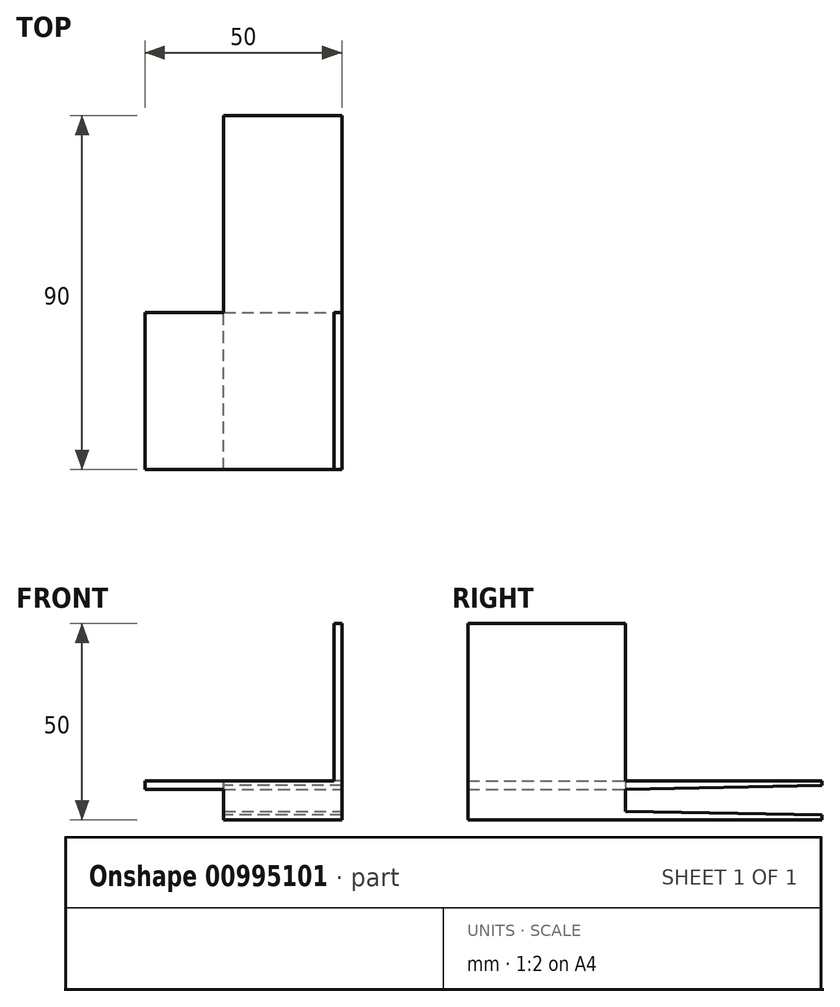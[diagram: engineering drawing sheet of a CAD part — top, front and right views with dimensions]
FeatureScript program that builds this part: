
annotation { "Feature Type Name" : "Feature", "Feature Type Description" : "" }
export const myFeature = defineFeature(function(context is Context, id is Id, definition is map)
    precondition{}
    {
        {
            var Q0;
            Q0=qCreatedBy(makeId("Front.planeOp"),FACE);
            var sketch = newSketch(context, id + "F0", { "sketchPlane" : qUnion([Q0])});
            skLineSegment(sketch, "E0.bottom", {"start": v(0, 0) * mm, "end": v(30, 0) * mm});
            skLineSegment(sketch, "E0.top", {"start": v(0, 10) * mm, "end": v(30, 10) * mm});
            skLineSegment(sketch, "E0.left", {"start": v(0, 0) * mm, "end": v(0, 10) * mm});
            skLineSegment(sketch, "E0.right", {"start": v(30, 0) * mm, "end": v(30, 10) * mm});
            skSolve(sketch);
        }
        {
            var Q0;
            Q0=qSketchRegion(id+"F0",true);
            extrude(context, id + "F1", {"entities" : qUnion([Q0]), "depth" : 40 * mm, "offsetDistance" : 25 * mm});
        }
        {
            var Q0;
            Q0=makeQuery(id+"F1.opExtrude","CAP_FACE",FACE,{"disambiguationData":[OSD([sQuery(id+"F0.wireOp",EDGE,"E0.bottom"),sQuery(id+"F0.wireOp",EDGE,"E0.top"),sQuery(id+"F0.wireOp",EDGE,"E0.left"),sQuery(id+"F0.wireOp",EDGE,"E0.right")])],"isStart":true});
            var sketch = newSketch(context, id + "F2", { "sketchPlane" : qUnion([Q0])});
            skLineSegment(sketch, "E1.bottom", {"start": v(0, 0) * mm, "end": v(-30, 0) * mm});
            skLineSegment(sketch, "E1.top", {"start": v(0, 2.25) * mm, "end": v(-30, 2.25) * mm});
            skLineSegment(sketch, "E1.left", {"start": v(0, 0) * mm, "end": v(0, 2.25) * mm});
            skLineSegment(sketch, "E1.right", {"start": v(-30, 0) * mm, "end": v(-30, 2.25) * mm});
            skLineSegment(sketch, "E2.bottom", {"start": v(0, 10) * mm, "end": v(-30, 10) * mm});
            skLineSegment(sketch, "E2.top", {"start": v(0, 7.75) * mm, "end": v(-30, 7.75) * mm});
            skLineSegment(sketch, "E2.left", {"start": v(0, 10) * mm, "end": v(0, 7.75) * mm});
            skLineSegment(sketch, "E2.right", {"start": v(-30, 10) * mm, "end": v(-30, 7.75) * mm});
            skLineSegment(sketch, "E3", {"start": v(0, 2.25) * mm, "end": v(0, 7.75) * mm});
            skSolve(sketch);
        }
        {
            var Q0;
            Q0=qSketchRegion(id+"F2",true);
            extrude(context, id + "F3", {"entities" : qUnion([Q0]), "operationType" : NewBodyOperationType.ADD, "depth" : 50 * mm, "offsetDistance" : 25 * mm});
        }
        {
            var Q0;
            Q0=makeQuery(id+"F3.boolean.opBoolean","MERGE",FACE,{"derivedFrom":[makeQuery(id+"F1.opExtrude","SWEPT_FACE",FACE,{"disambiguationData":[OSD([sQuery(id+"F0.wireOp",EDGE,"E0.left")])]}),makeQuery(id+"F3.opExtrude","SWEPT_FACE",FACE,{"disambiguationData":[OSD([sQuery(id+"F2.wireOp",EDGE,"E1.left")])]}),makeQuery(id+"F3.opExtrude","SWEPT_FACE",FACE,{"disambiguationData":[OSD([sQuery(id+"F2.wireOp",EDGE,"E2.left")])]})]});
            var sketch = newSketch(context, id + "F4", { "sketchPlane" : qUnion([Q0])});
            skLineSegment(sketch, "E4", {"start": v(0, 7.75) * mm, "end": v(-50, 8.75) * mm});
            skLineSegment(sketch, "E5", {"start": v(-50, 8.75) * mm, "end": v(-50, 7.75) * mm});
            skLineSegment(sketch, "E6", {"start": v(-50, 7.75) * mm, "end": v(0, 7.75) * mm});
            skLineSegment(sketch, "E7", {"start": v(0, 2.25) * mm, "end": v(-50, 1.25) * mm});
            skLineSegment(sketch, "E8", {"start": v(-50, 1.25) * mm, "end": v(-50, 2.25) * mm});
            skLineSegment(sketch, "E9", {"start": v(-50, 2.25) * mm, "end": v(0, 2.25) * mm});
            skSolve(sketch);
        }
        {
            var Q0;
            Q0=qSketchRegion(id+"F4",true);
            extrude(context, id + "F5", {"entities" : qUnion([Q0]), "operationType" : NewBodyOperationType.REMOVE, "endBound" : BoundingType.UP_TO_NEXT, "oppositeDirection" : true, "depth" : 25 * mm, "offsetDistance" : 25 * mm});
        }
        {
            var Q0;
            Q0=makeQuery(id+"F3.boolean.opBoolean","MERGE",FACE,{"derivedFrom":[makeQuery(id+"F1.opExtrude","SWEPT_FACE",FACE,{"disambiguationData":[OSD([sQuery(id+"F0.wireOp",EDGE,"E0.left")])]}),makeQuery(id+"F3.opExtrude","SWEPT_FACE",FACE,{"disambiguationData":[OSD([sQuery(id+"F2.wireOp",EDGE,"E1.left")])]}),makeQuery(id+"F3.opExtrude","SWEPT_FACE",FACE,{"disambiguationData":[OSD([sQuery(id+"F2.wireOp",EDGE,"E2.left")])]})]});
            var sketch = newSketch(context, id + "F6", { "sketchPlane" : qUnion([Q0])});
            skLineSegment(sketch, "E10.bottom", {"start": v(40, 10) * mm, "end": v(0, 10) * mm});
            skLineSegment(sketch, "E10.top", {"start": v(40, 7.75) * mm, "end": v(0, 7.75) * mm});
            skLineSegment(sketch, "E10.left", {"start": v(40, 10) * mm, "end": v(40, 7.75) * mm});
            skLineSegment(sketch, "E10.right", {"start": v(0, 10) * mm, "end": v(0, 7.75) * mm});
            skSolve(sketch);
        }
        {
            var Q0;
            Q0 = qSketchRegion(id + "F6", true);
            extrude(context, id + "F7", {"entities" : qUnion([Q0]), "operationType" : NewBodyOperationType.ADD, "depth" : 20 * mm, "offsetDistance" : 25 * mm});
        }
        {
            var Q0;
            Q0=makeQuery(id+"F7.boolean.opBoolean","MERGE",FACE,{"derivedFrom":[makeQuery(id+"F3.boolean.opBoolean","MERGE",FACE,{"derivedFrom":[makeQuery(id+"F1.opExtrude","SWEPT_FACE",FACE,{"disambiguationData":[OSD([sQuery(id+"F0.wireOp",EDGE,"E0.top")])]}),makeQuery(id+"F3.opExtrude","SWEPT_FACE",FACE,{"disambiguationData":[OSD([sQuery(id+"F2.wireOp",EDGE,"E2.bottom")])]})]}),makeQuery(id+"F7.opExtrude","SWEPT_FACE",FACE,{"disambiguationData":[OSD([sQuery(id+"F6.wireOp",EDGE,"E10.bottom")])]})]});
            var sketch = newSketch(context, id + "F8", { "sketchPlane" : qUnion([Q0])});
            skLineSegment(sketch, "E11.bottom", {"start": v(30, -40) * mm, "end": v(28, -40) * mm});
            skLineSegment(sketch, "E11.top", {"start": v(30, 0) * mm, "end": v(28, 0) * mm});
            skLineSegment(sketch, "E11.left", {"start": v(30, -40) * mm, "end": v(30, 0) * mm});
            skLineSegment(sketch, "E11.right", {"start": v(28, -40) * mm, "end": v(28, 0) * mm});
            skSolve(sketch);
        }
        {
            var Q0;
            Q0 = qSketchRegion(id + "F8", true);
            extrude(context, id + "F9", {"entities" : qUnion([Q0]), "operationType" : NewBodyOperationType.ADD, "depth" : 40 * mm, "offsetDistance" : 25 * mm});
        }
    });
